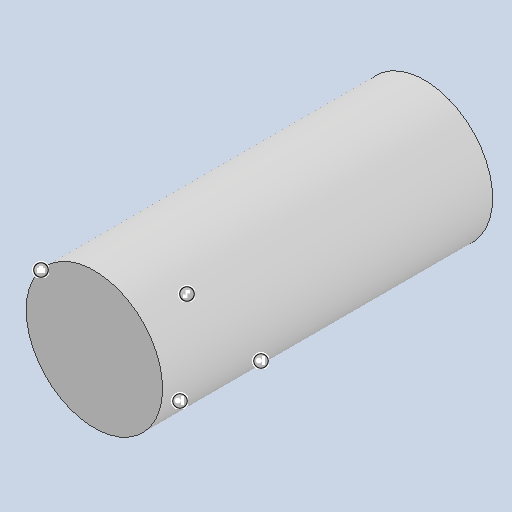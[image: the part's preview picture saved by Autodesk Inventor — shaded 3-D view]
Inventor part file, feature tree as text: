
AUTODESK INVENTOR PART (.ipt)
format: ipt  version: 2022 (Build 260153000, 153)  size: 98,304 bytes
history: native  units: mm
features: extrude x1, sketch x1
ambient origin geometry x8: Origin, YZ Plane, XZ Plane, XY Plane, X Axis, Y Axis, Z Axis, Center Point
bodies: Solid1 (feature_tree)
feature tree (2):
  extrude  "Extrusion1"  TaperAngle=0.0deg  [1 undecoded]
  sketch  "Sketch1"  dims[d2=0.0mm d3=0.0mm d4=0.0mm d9=0.0mm d10=0.0mm]
note: 1 required parameter value undecoded (feature->parameter linkage not recoverable at this tier; creation-order binding heuristic only, values carry confidence <= 0.55)
